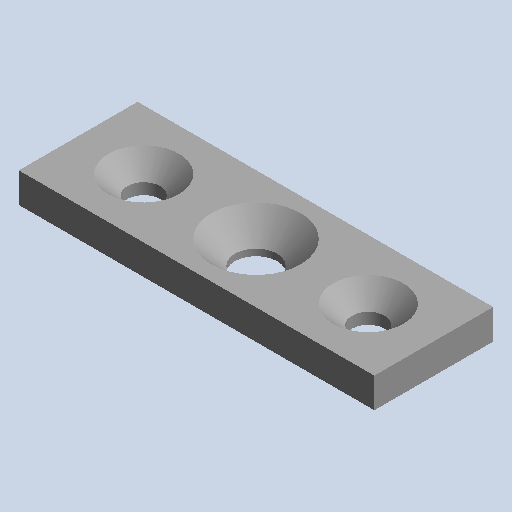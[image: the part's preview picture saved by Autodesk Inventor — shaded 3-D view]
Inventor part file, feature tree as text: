
AUTODESK INVENTOR PART (.ipt)
format: ipt  version: 2022.1 (Build 261234000, 234)  size: 69,120 bytes
history: native  units: mm (DEFAULTED — no unit token found)
features: other x8, chamfer x1
bodies: Body1 (feature_tree)
feature tree (9):
  other  "Sólido1"
  other  "Origen"
  other  "Plano YZ"
  other  "Plano XZ"
  other  "Plano XY"
  other  "Eje X"
  other  "Eje Y"
  other  "Eje Z"
  chamfer  "Chamfer2"  [1 undecoded]
note: 1 required parameter value undecoded (feature->parameter linkage not recoverable at this tier; creation-order binding heuristic only, values carry confidence <= 0.55)
